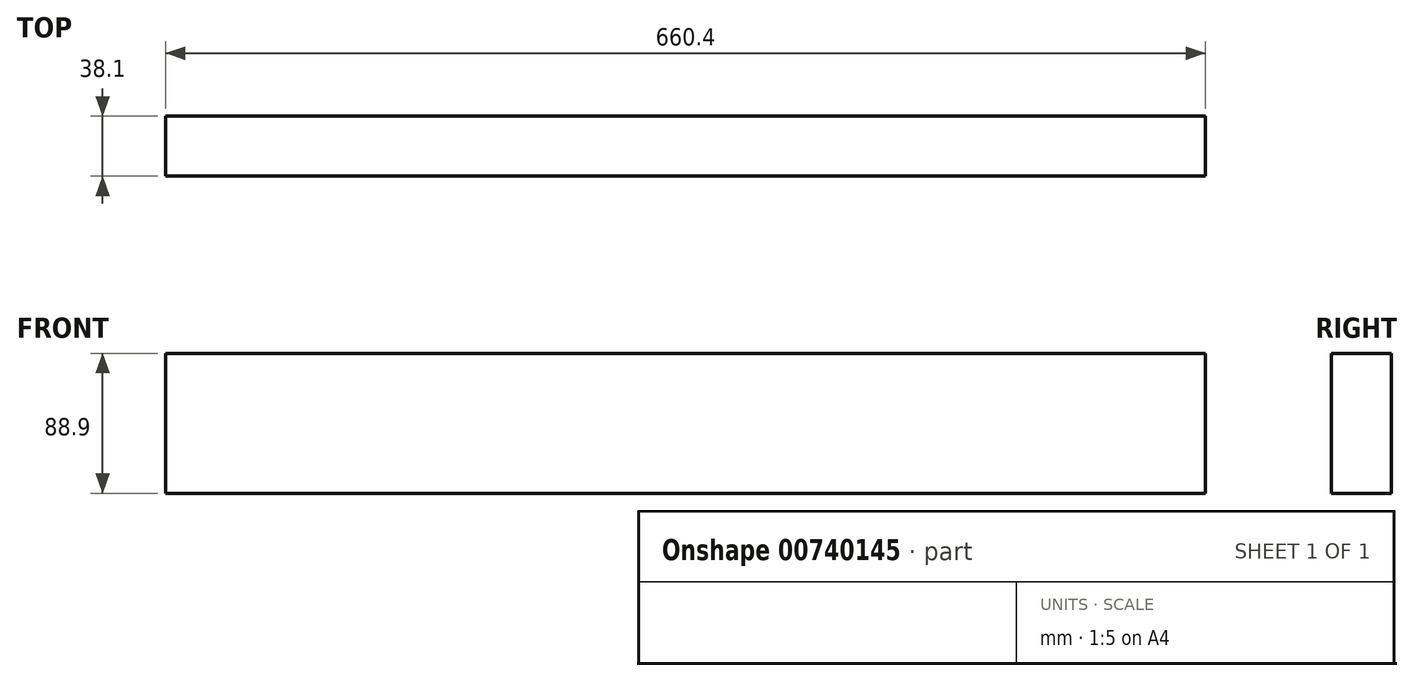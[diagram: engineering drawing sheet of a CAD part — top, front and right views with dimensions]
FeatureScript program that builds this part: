
annotation { "Feature Type Name" : "Feature", "Feature Type Description" : "" }
export const myFeature = defineFeature(function(context is Context, id is Id, definition is map)
    precondition{}
    {
        {
            var Q0;
            Q0=qCreatedBy(makeId("Right.planeOp"),FACE);
            var sketch = newSketch(context, id + "F0", { "sketchPlane" : qUnion([Q0])});
            skLineSegment(sketch, "E0.bottom", {"start": v(-79.68, 85.36) * mm, "end": v(-41.58, 85.36) * mm});
            skLineSegment(sketch, "E0.top", {"start": v(-79.68, -3.54) * mm, "end": v(-41.58, -3.54) * mm});
            skLineSegment(sketch, "E0.left", {"start": v(-79.68, 85.36) * mm, "end": v(-79.68, -3.54) * mm});
            skLineSegment(sketch, "E0.right", {"start": v(-41.58, 85.36) * mm, "end": v(-41.58, -3.54) * mm});
            skSolve(sketch);
        }
        {
            var Q0;
            Q0=makeQuery(id+"F0.imprint","IMPRINT",FACE,{"disambiguationData":[TD([[makeQuery(id+"F0.imprint","IMPRINT",EDGE,{"derivedFrom":sQuery(id+"F0.wireOp",EDGE,"E0.bottom")}),-1.0]])]});
            extrude(context, id + "F1", {"entities" : qUnion([Q0]), "depth" : 660.4 * mm, "offsetDistance" : 25.4 * mm});
        }
    });
